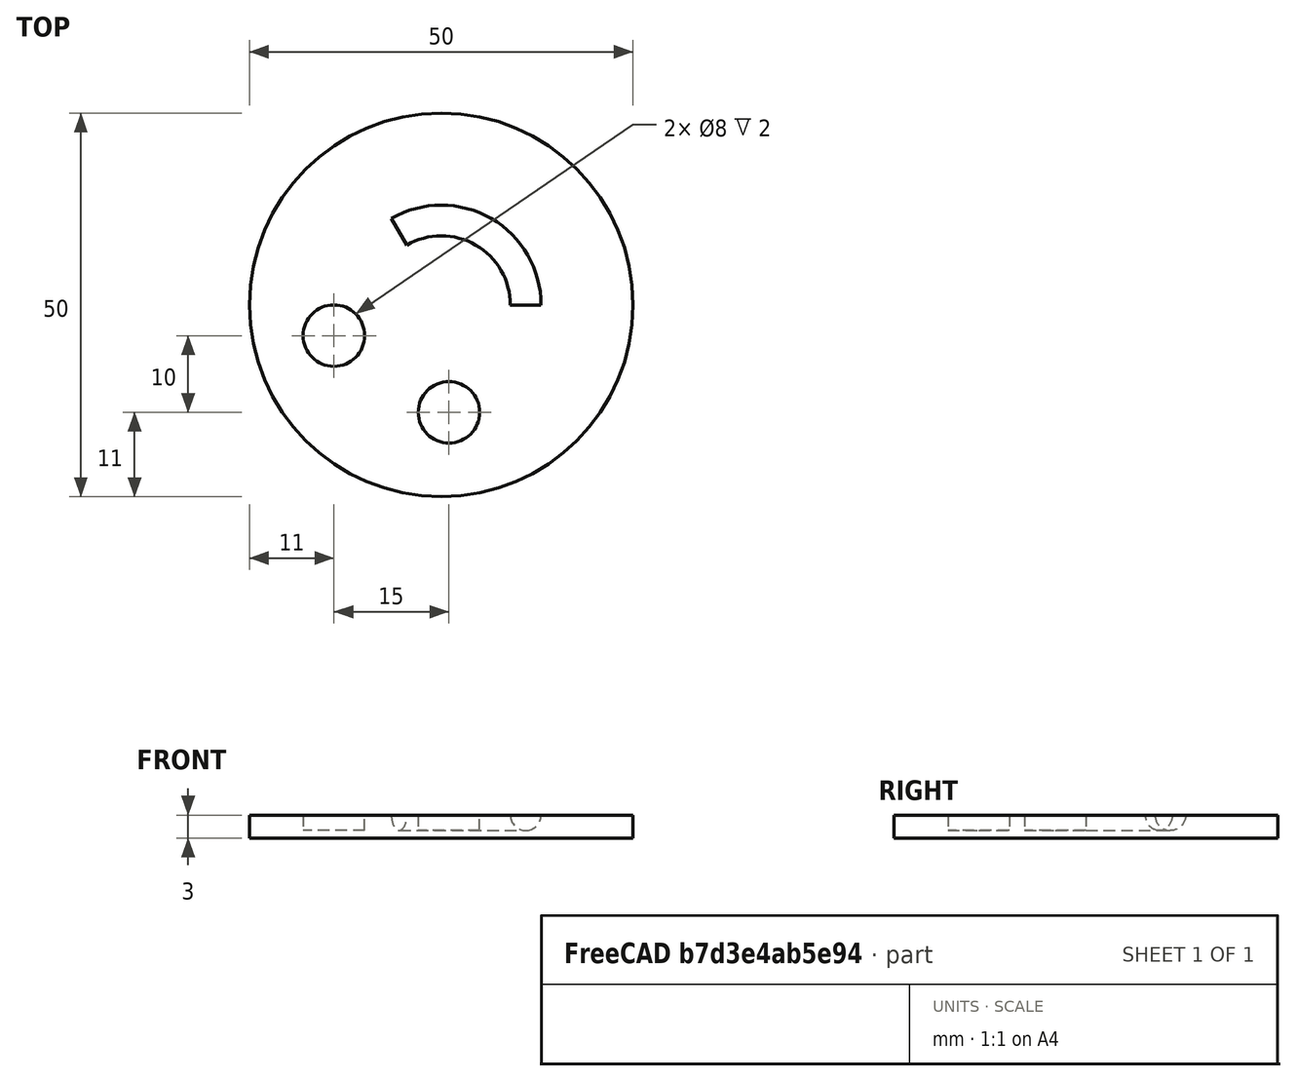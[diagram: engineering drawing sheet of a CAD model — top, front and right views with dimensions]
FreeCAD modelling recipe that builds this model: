
FCSTD DOCUMENT  (FreeCAD 0.21R33771 (Git))
Label: OJT1_T15R01_smiley
License: All rights reserved
LicenseURL: http://en.wikipedia.org/wiki/All_rights_reserved
objects: Part::Cylinder×3, Part::Torus×1, Part::MultiFuse×1, Part::Cut×1
note: 6 computed .brp shape members not serialized (recipe doc carries the construction recipe); baked Part::Feature solids carry a one-line shape summary decoded from their .brp

FEATURE [Part::Cylinder] Cylinder
  Angle = 360
  AttacherType = Attacher::AttachEngine3D
  FirstAngle = 0
  Height = 3
  Radius = 25
  SecondAngle = 0
FEATURE [Part::Torus] Torus
  Angle1 = -180
  Angle2 = 180
  Angle3 = 120
  AttacherType = Attacher::AttachEngine3D
  Placement = pos=(0,0,3) rot=(0,0,1;0rad)
  Radius1 = 11
  Radius2 = 2
FEATURE [Part::Cylinder] Cylinder001  label="eye"
  Angle = 360
  AttacherType = Attacher::AttachEngine3D
  FirstAngle = 0
  Height = 10
  Placement = pos=(1,-14,1) rot=(0,0,1;0rad)
  Radius = 4
  SecondAngle = 0
FEATURE [Part::Cylinder] Cylinder002  label="eye001"
  Angle = 360
  AttacherType = Attacher::AttachEngine3D
  FirstAngle = 0
  Height = 10
  Placement = pos=(-14,-4,1) rot=(0,0,1;0rad)
  Radius = 4
  SecondAngle = 0
FEATURE [Part::MultiFuse] Fusion
  Refine = true
  Shapes = -> [Torus,Cylinder001,Cylinder002]
FEATURE [Part::Cut] Cut  label="smiley"
  Base = -> Cylinder
  Refine = true
  Tool = -> Fusion
